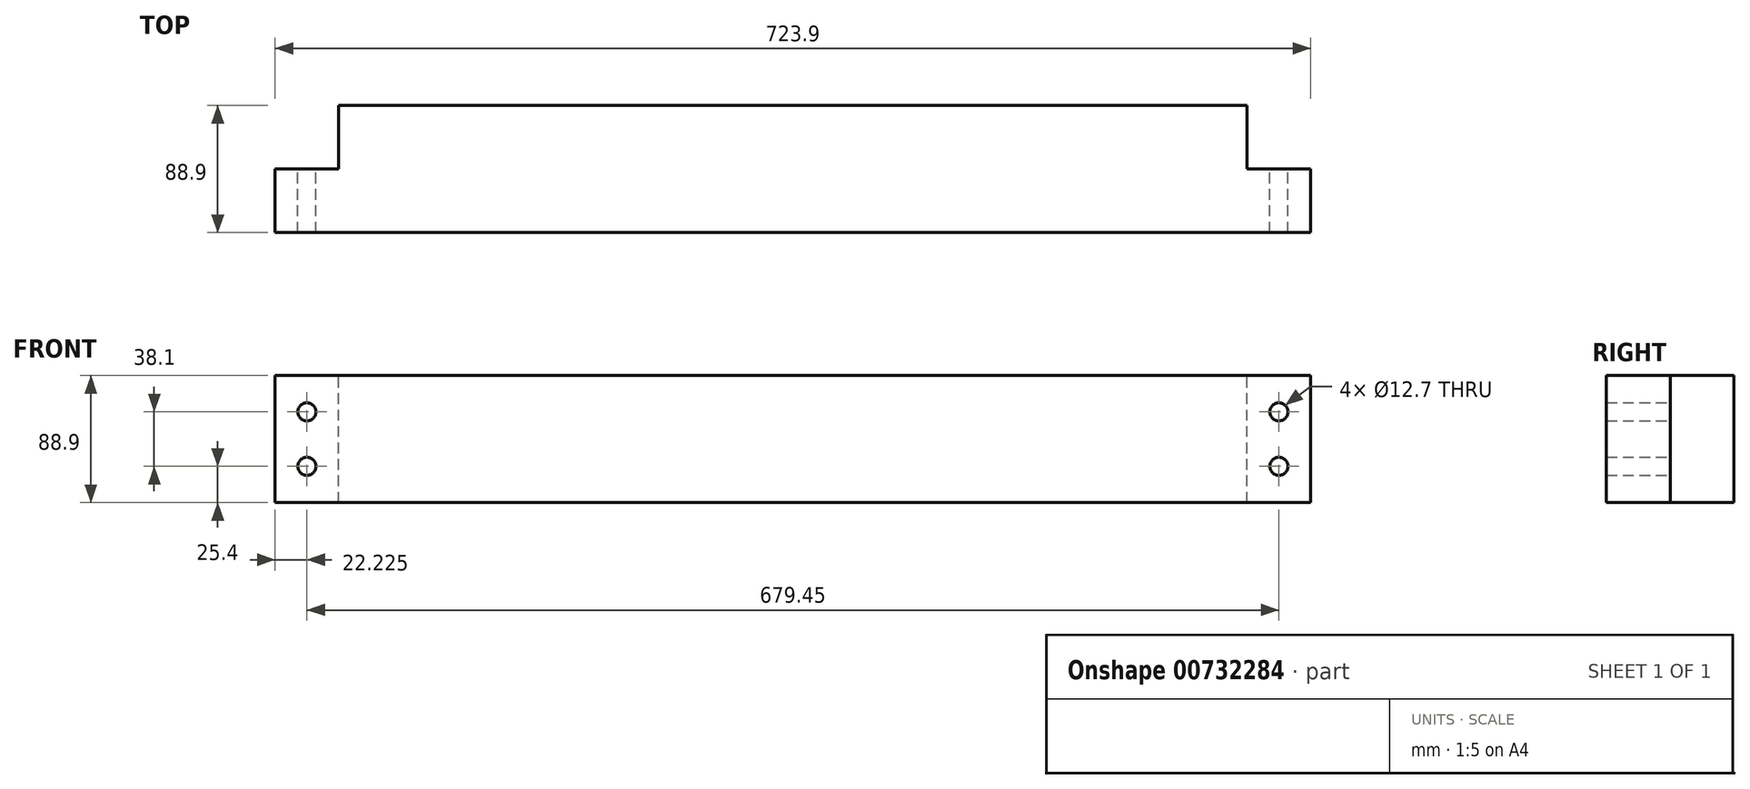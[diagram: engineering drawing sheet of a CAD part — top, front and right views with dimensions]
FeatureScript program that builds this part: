
annotation { "Feature Type Name" : "Feature", "Feature Type Description" : "" }
export const myFeature = defineFeature(function(context is Context, id is Id, definition is map)
    precondition{}
    {
        {
            var Q0;
            Q0=qCreatedBy(makeId("Front.planeOp"),FACE);
            var sketch = newSketch(context, id + "F0", { "sketchPlane" : qUnion([Q0])});
            skLineSegment(sketch, "E0.bottom", {"start": v(361.95, 44.45) * mm, "end": v(-361.95, 44.45) * mm});
            skLineSegment(sketch, "E0.top", {"start": v(361.95, -44.45) * mm, "end": v(-361.95, -44.45) * mm});
            skLineSegment(sketch, "E0.left", {"start": v(361.95, 44.45) * mm, "end": v(361.95, -44.45) * mm});
            skLineSegment(sketch, "E0.right", {"start": v(-361.95, 44.45) * mm, "end": v(-361.95, -44.45) * mm});
            skPoint(sketch, "E0.middle", {"position": v(0, 0) * mm});
            skLineSegment(sketch, "E1", {"start": v(-361.95, 0) * mm, "end": v(361.95, 0) * mm, "construction": true});
            skLineSegment(sketch, "E2", {"start": v(317.5, 44.45) * mm, "end": v(317.5, -44.45) * mm, "construction": true});
            skLineSegment(sketch, "E3", {"start": v(-317.5, 44.45) * mm, "end": v(-317.5, -44.45) * mm, "construction": true});
            skLineSegment(sketch, "E4", {"start": v(-339.73, -44.45) * mm, "end": v(-339.73, 44.45) * mm, "construction": true});
            skLineSegment(sketch, "E5", {"start": v(339.73, 44.45) * mm, "end": v(339.73, -44.45) * mm, "construction": true});
            skLineSegment(sketch, "E6", {"start": v(-361.95, 19.05) * mm, "end": v(361.95, 19.05) * mm, "construction": true});
            skLineSegment(sketch, "E7", {"start": v(361.95, -19.05) * mm, "end": v(-361.95, -19.05) * mm, "construction": true});
            skCircle(sketch, "E8", {"center": v(-339.73, 19.05) * mm, "radius": 6.35 * mm});
            skCircle(sketch, "E9", {"center": v(-339.73, -19.05) * mm, "radius": 6.35 * mm});
            skCircle(sketch, "E10", {"center": v(339.73, -19.05) * mm, "radius": 6.35 * mm});
            skCircle(sketch, "E11", {"center": v(339.73, 19.05) * mm, "radius": 6.35 * mm});
            skSolve(sketch);
        }
        {
            var Q0;
            Q0=makeQuery(id+"F0.imprint","IMPRINT",FACE,{"disambiguationData":[TD([[makeQuery(id+"F0.imprint","IMPRINT",EDGE,{"derivedFrom":sQuery(id+"F0.wireOp",EDGE,"E0.bottom")}),1.0]])]});
            extrude(context, id + "F1", {"entities" : qUnion([Q0]), "depth" : 88.9 * mm, "offsetDistance" : 25.4 * mm});
        }
        {
            var Q0;
            Q0=makeQuery(id+"F1.opExtrude","SWEPT_FACE",FACE,{"disambiguationData":[OSD([sQuery(id+"F0.wireOp",EDGE,"E0.bottom")])]});
            var sketch = newSketch(context, id + "F2", { "sketchPlane" : qUnion([Q0])});
            skLineSegment(sketch, "E12", {"start": v(-361.95, -44.45) * mm, "end": v(361.95, -44.45) * mm, "construction": true});
            skLineSegment(sketch, "E13", {"start": v(-317.5, 0) * mm, "end": v(-317.5, -44.45) * mm, "construction": true});
            skLineSegment(sketch, "E14", {"start": v(317.5, 0) * mm, "end": v(317.5, -44.45) * mm, "construction": true});
            skLineSegment(sketch, "E15.bottom", {"start": v(-361.95, 0) * mm, "end": v(-317.5, 0) * mm});
            skLineSegment(sketch, "E15.top", {"start": v(-361.95, -44.45) * mm, "end": v(-317.5, -44.45) * mm});
            skLineSegment(sketch, "E15.left", {"start": v(-361.95, 0) * mm, "end": v(-361.95, -44.45) * mm});
            skLineSegment(sketch, "E15.right", {"start": v(-317.5, 0) * mm, "end": v(-317.5, -44.45) * mm});
            skLineSegment(sketch, "E16.bottom", {"start": v(317.5, 0) * mm, "end": v(361.95, 0) * mm});
            skLineSegment(sketch, "E16.top", {"start": v(317.5, -44.45) * mm, "end": v(361.95, -44.45) * mm});
            skLineSegment(sketch, "E16.left", {"start": v(317.5, 0) * mm, "end": v(317.5, -44.45) * mm});
            skLineSegment(sketch, "E16.right", {"start": v(361.95, 0) * mm, "end": v(361.95, -44.45) * mm});
            skSolve(sketch);
        }
        {
            var Q0;
            Q0=makeQuery(id+"F2.imprint","IMPRINT",FACE,{"disambiguationData":[TD([[makeQuery(id+"F2.imprint","IMPRINT",EDGE,{"derivedFrom":sQuery(id+"F2.wireOp",EDGE,"E15.bottom")}),1.0]])]});
            var Q1;
            Q1=makeQuery(id+"F2.imprint","IMPRINT",FACE,{"disambiguationData":[TD([[makeQuery(id+"F2.imprint","IMPRINT",EDGE,{"derivedFrom":sQuery(id+"F2.wireOp",EDGE,"E16.bottom")}),1.0]])]});
            extrude(context, id + "F3", {"entities" : qUnion([Q0, Q1]), "operationType" : NewBodyOperationType.REMOVE, "oppositeDirection" : true, "depth" : 101.6 * mm, "offsetDistance" : 25.4 * mm});
        }
    });
